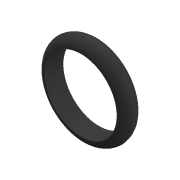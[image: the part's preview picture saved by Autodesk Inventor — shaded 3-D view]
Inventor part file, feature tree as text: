
AUTODESK INVENTOR PART (.ipt)
format: ipt  version: 2020 (Build 240168000, 168)  size: 126,464 bytes
history: native  units: mm
features: other x1, extrude x1, fillet x1, sketch x1
ambient origin geometry x8: Origin, YZ Plane, XZ Plane, XY Plane, X Axis, Y Axis, Z Axis, Center Point
bodies: Body1 (feature_tree)
feature tree (4):
  other  "솔리드1"
  extrude  "돌출1"  Depth=120.0mm
  fillet  "모깎기1"  Radius=150.0mm
  sketch  "스케치1"
